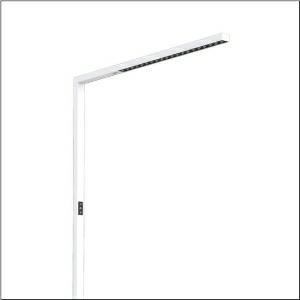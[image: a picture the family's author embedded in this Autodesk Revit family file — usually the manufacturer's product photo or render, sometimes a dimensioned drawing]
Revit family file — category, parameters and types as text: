
# Revit family: silica_r__31_floor_51my52fa3cw_3d14
name_source: partatom
category: Lighting Fixtures
units: mm (PartAtom-declared; Revit-internal decimal feet)

## family parameters
Cut with Voids When Loaded = No
Host = Face
Light Source = No
Part Type = Normal
Room Calculation Point = No
Round Connector Dimension = Use Diameter
Shared = No

## types (1)
- Silica® 31 Floor (1 x LED, 10300 lm, 75 W, 3000K)
    Apparent Load = 75 VA
    CIE Flux Codes = 86 100 100 24 100
    Color Rendering = 80
    Color Temperature = 3000K
    Default Elevation = 1800 mm
    Description = Silica® 31 Floor, floorstanding luminaire, secondary optical cover: cover panel, of PMMA, light emission: direct/indirect distribution, primary light characteristic: symmetric, installation type: not mounted, LED, rated luminous flux: 10.300lm, luminous efficacy: 137lm/W, light colour: 830, colour temperature: 3000K, control gear: Touchdim, daylight-dependent control, with cable with plug, mains connection: 230V, AC, 50Hz, connection cable pre-assembled, rated input power: 75W, luminaire head, of aluminium, traffic white (RAL 9016), length: 1.203mm, width: 52mm, supporting column, angular, of aluminium, traffic white (RAL 9016), baseplate, of steel, traffic white (RAL 9016), protection rating (complete): IP20, insulation class (complete): insulation class I (protective earthing), certification: CE, permissible operating ambient temperature: -20..+40°C, standard: EN 50419, packaging unit: 1 piece
    Height = 36 mm
    Lamp = 1 x LED
    Lamp Light Flux = 10300 lm
    Lamp Power = 75 W
    Lamp count = 1
    Length = 1203 mm
    Luminous efficacy = 137 lm/W
    Manufacturer = Siteco
    ModVariant = No
    Model = 51MY52FA3CW
    Mounting Place = Floor
    Mounting Type = Freestanding
    Number of Poles = 1
    OnlyDefault = Yes
    Power Factor = 1
    Product Name = Silica® 31 Floor
    Product group = floorstanding luminaire
    ProductGroupID = 1302
    Protection Class = Protection class I
    Protection Degree = IP 20
    RLX_Detail_Level = 1
    RLX_Emergency_Light_Flux = 0 lm
    RLX_Emergency_Type = 0
    RLX_Emergency_Type_DB = No
    RlxData = <blob elided: 17165 chars, md5=3739ba2d>
    Socket = socket
    Standby Power = 0 W
    System Light Flux = 10300 lm
    System Power = 75 W
    Type Comments = Product without accessories
    Type Image = l_1275309.jpg
    URL = http://relux.com
    VarID = ---
    Voltage = 0 V
    Weight = 0.00 kg
    Width = 52 mm  [stored 0.170604 ft]

note: [stored X ft] marks values corroborated as IEEE doubles in the binary element streams (Revit-internal decimal feet)

## geometry (parser evidence)
native form markers: Blend x4, Sweep x15
no freeform markers — native parametric forms only
